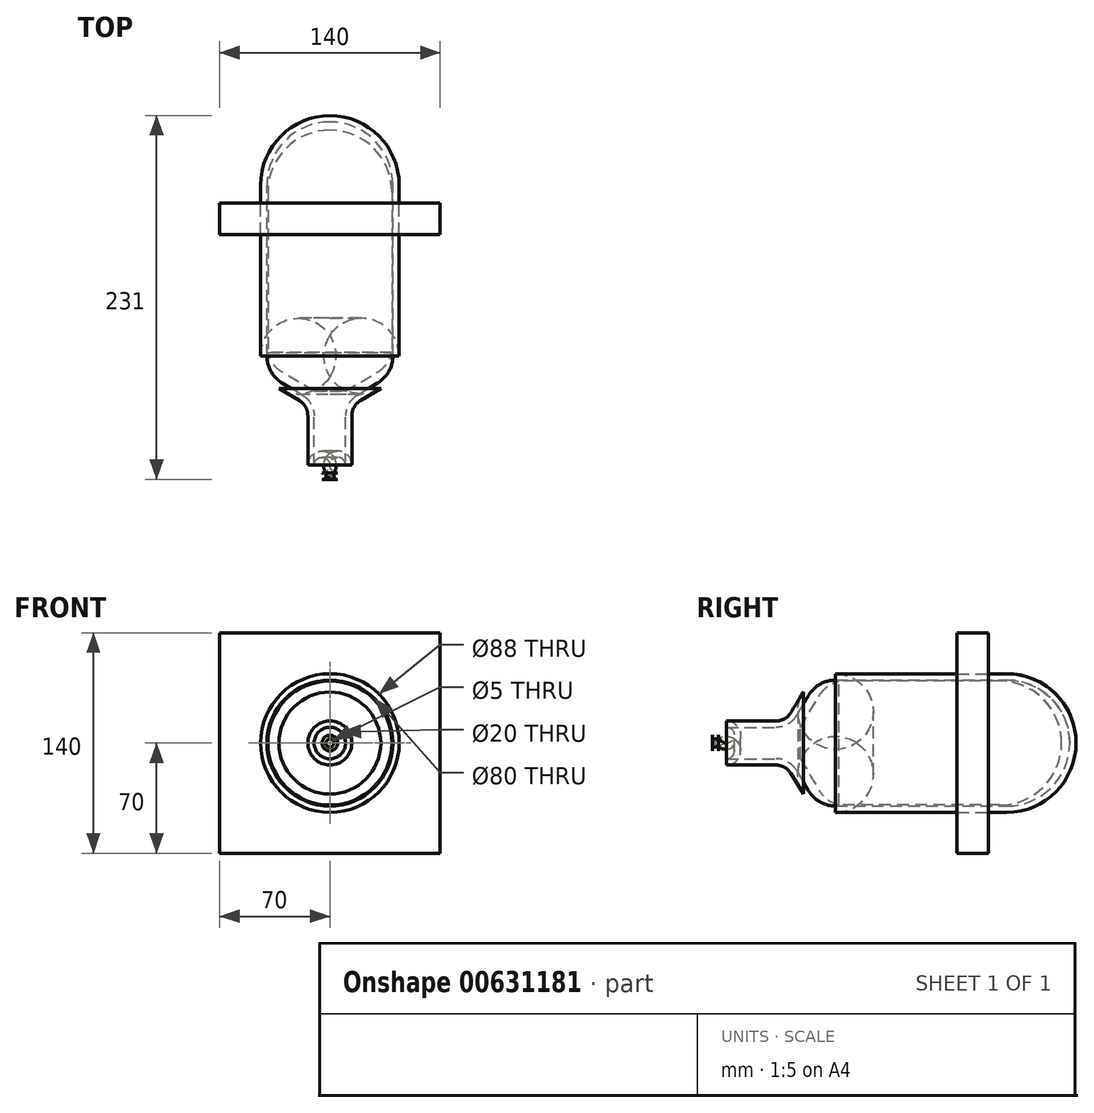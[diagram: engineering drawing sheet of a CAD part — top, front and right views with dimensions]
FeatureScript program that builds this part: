
annotation { "Feature Type Name" : "Feature", "Feature Type Description" : "" }
export const myFeature = defineFeature(function(context is Context, id is Id, definition is map)
    precondition{}
    {
        {
            var Q0;
            Q0=qCreatedBy(makeId("Right.planeOp"),FACE);
            var sketch = newSketch(context, id + "F0", { "sketchPlane" : qUnion([Q0])});
            skLineSegment(sketch, "E0", {"start": v(-160.68, 40) * mm, "end": v(-52, 40) * mm});
            skLineSegment(sketch, "E1", {"start": v(-160.68, -40) * mm, "end": v(-52, -40) * mm});
            skArc(sketch, "E2", {"start": v(-52, -40) * mm, "mid": v(-12, 0) * mm, "end": v(-52, 40) * mm});
            skPoint(sketch, "E3", {"position": v(-12, 0) * mm});
            skLineSegment(sketch, "E4", {"start": v(-177.83, 30.29) * mm, "end": v(-185.63, 17.28) * mm});
            skLineSegment(sketch, "E5", {"start": v(-198.5, 10) * mm, "end": v(-230, 10) * mm});
            skLineSegment(sketch, "E6", {"start": v(-235, 5) * mm, "end": v(-235, 2.5) * mm});
            skLineSegment(sketch, "E7", {"start": v(-230, -10) * mm, "end": v(-198.5, -10) * mm});
            skLineSegment(sketch, "E8", {"start": v(-185.63, -17.28) * mm, "end": v(-177.83, -30.29) * mm});
            skPoint(sketch, "E9.visualSharp", {"position": v(-172, 40) * mm});
            skArc(sketch, "E9.filletArc", {"start": v(-160.68, 40) * mm, "mid": v(-170.53, 37.4) * mm, "end": v(-177.83, 30.29) * mm});
            skPoint(sketch, "E10.visualSharp", {"position": v(-172, -40) * mm});
            skArc(sketch, "E10.filletArc", {"start": v(-177.83, -30.29) * mm, "mid": v(-170.53, -37.4) * mm, "end": v(-160.68, -40) * mm});
            skPoint(sketch, "E11.visualSharp", {"position": v(-190, 10) * mm});
            skArc(sketch, "E11.filletArc", {"start": v(-198.5, 10) * mm, "mid": v(-191.1, 11.95) * mm, "end": v(-185.63, 17.28) * mm});
            skPoint(sketch, "E12.visualSharp", {"position": v(-190, -10) * mm});
            skArc(sketch, "E12.filletArc", {"start": v(-185.63, -17.28) * mm, "mid": v(-191.1, -11.95) * mm, "end": v(-198.5, -10) * mm});
            skPoint(sketch, "E13.visualSharp", {"position": v(-235, 10) * mm});
            skArc(sketch, "E13.filletArc", {"start": v(-230, 10) * mm, "mid": v(-233.54, 8.54) * mm, "end": v(-235, 5) * mm});
            skPoint(sketch, "E14.visualSharp", {"position": v(-235, -10) * mm});
            skArc(sketch, "E14.filletArc", {"start": v(-235, -5) * mm, "mid": v(-233.54, -8.54) * mm, "end": v(-230, -10) * mm});
            skPoint(sketch, "E15", {"position": v(-235, 2.5) * mm});
            skPoint(sketch, "E16", {"position": v(-235, 0) * mm});
            skPoint(sketch, "E17", {"position": v(-235, -2.5) * mm});
            skLineSegment(sketch, "E18.trimOffspring", {"start": v(-235, -2.5) * mm, "end": v(-235, -5) * mm});
            skLineSegment(sketch, "E19.0", {"start": v(-239, 5) * mm, "end": v(-239, 2.5) * mm});
            skArc(sketch, "E19.1", {"start": v(-230, 14) * mm, "mid": v(-236.36, 11.36) * mm, "end": v(-239, 5) * mm});
            skLineSegment(sketch, "E19.2", {"start": v(-198.5, 14) * mm, "end": v(-230, 14) * mm});
            skArc(sketch, "E19.3", {"start": v(-198.5, 14) * mm, "mid": v(-193.07, 15.43) * mm, "end": v(-189.06, 19.34) * mm});
            skLineSegment(sketch, "E19.4", {"start": v(-181.26, 32.35) * mm, "end": v(-189.06, 19.34) * mm});
            skArc(sketch, "E19.5", {"start": v(-189.06, -19.34) * mm, "mid": v(-193.07, -15.43) * mm, "end": v(-198.5, -14) * mm});
            skLineSegment(sketch, "E19.6", {"start": v(-230, -14) * mm, "end": v(-198.5, -14) * mm});
            skArc(sketch, "E19.7", {"start": v(-239, -5) * mm, "mid": v(-236.36, -11.36) * mm, "end": v(-230, -14) * mm});
            skLineSegment(sketch, "E19.8", {"start": v(-239, -2.5) * mm, "end": v(-239, -5) * mm});
            skLineSegment(sketch, "E19.9", {"start": v(-189.06, -19.34) * mm, "end": v(-181.26, -32.35) * mm});
            skArc(sketch, "E19.10", {"start": v(-181.26, -32.35) * mm, "mid": v(-172.5, -40.88) * mm, "end": v(-160.68, -44) * mm});
            skLineSegment(sketch, "E19.11", {"start": v(-160.68, -44) * mm, "end": v(-52, -44) * mm});
            skArc(sketch, "E19.12", {"start": v(-52, -44) * mm, "mid": v(-8, 0) * mm, "end": v(-52, 44) * mm});
            skLineSegment(sketch, "E19.13", {"start": v(-160.68, 44) * mm, "end": v(-52, 44) * mm});
            skArc(sketch, "E19.14", {"start": v(-160.68, 44) * mm, "mid": v(-172.5, 40.88) * mm, "end": v(-181.26, 32.35) * mm});
            skLineSegment(sketch, "E20", {"start": v(-239, 2.5) * mm, "end": v(-235, 2.5) * mm});
            skLineSegment(sketch, "E21", {"start": v(-239, -2.5) * mm, "end": v(-235, -2.5) * mm});
            skLineSegment(sketch, "E22", {"start": v(-52, 0) * mm, "end": v(-72, 0) * mm, "construction": true});
            skLineSegment(sketch, "E23", {"start": v(-12, 0) * mm, "end": v(-8, 0) * mm});
            skPoint(sketch, "E24", {"position": v(0, 0) * mm});
            skSolve(sketch);
        }
        {
            var Q0;
            {var subQ3=sQuery(id+"F0.wireOp",EDGE,"E0");Q0=makeQuery(id+"F0.imprint","IMPRINT",FACE,{"disambiguationData":[TD([[makeQuery(id+"F0.imprint","IMPRINT",EDGE,{"derivedFrom":subQ3}),1.0]])]});}
            var Q1;
            Q1=sQuery(id+"F0.wireOp",EDGE,"E22");
            revolve(context, id + "F1", {"entities" : qUnion([Q0]), "axis" : qUnion([Q1]), "revolveType" : RevolveType.FULL});
        }
        {
            var Q0;
            Q0=qCreatedBy(makeId("Right.planeOp"),FACE);
            var sketch = newSketch(context, id + "F2", { "sketchPlane" : qUnion([Q0])});
            skLineSegment(sketch, "E25", {"start": v(-153.75, 40) * mm, "end": v(-52, 40) * mm, "construction": true});
            skLineSegment(sketch, "E26", {"start": v(-153.75, -40) * mm, "end": v(-52, -40) * mm, "construction": true});
            skArc(sketch, "E27", {"start": v(-52, -40) * mm, "mid": v(-12, 0) * mm, "end": v(-52, 40) * mm, "construction": true});
            skPoint(sketch, "E28", {"position": v(-12, 0) * mm});
            skLineSegment(sketch, "E29", {"start": v(-177.83, 30.29) * mm, "end": v(-185.63, 17.28) * mm, "construction": true});
            skLineSegment(sketch, "E30", {"start": v(-198.5, 10) * mm, "end": v(-230, 10) * mm, "construction": true});
            skLineSegment(sketch, "E31", {"start": v(-235, 5) * mm, "end": v(-235, 2.5) * mm, "construction": true});
            skLineSegment(sketch, "E32", {"start": v(-230, -10) * mm, "end": v(-198.5, -10) * mm, "construction": true});
            skLineSegment(sketch, "E33", {"start": v(-185.63, -17.28) * mm, "end": v(-177.83, -30.29) * mm, "construction": true});
            skPoint(sketch, "E34.visualSharp", {"position": v(-172, 40) * mm});
            skArc(sketch, "E34.filletArc", {"start": v(-160.68, 40) * mm, "mid": v(-170.53, 37.4) * mm, "end": v(-177.83, 30.29) * mm, "construction": true});
            skPoint(sketch, "E35.visualSharp", {"position": v(-172, -40) * mm});
            skArc(sketch, "E35.filletArc", {"start": v(-177.83, -30.29) * mm, "mid": v(-170.53, -37.4) * mm, "end": v(-160.68, -40) * mm, "construction": true});
            skPoint(sketch, "E36.visualSharp", {"position": v(-190, 10) * mm});
            skArc(sketch, "E36.filletArc", {"start": v(-198.5, 10) * mm, "mid": v(-191.1, 11.95) * mm, "end": v(-185.63, 17.28) * mm, "construction": true});
            skPoint(sketch, "E37.visualSharp", {"position": v(-190, -10) * mm});
            skArc(sketch, "E37.filletArc", {"start": v(-185.63, -17.28) * mm, "mid": v(-191.1, -11.95) * mm, "end": v(-198.5, -10) * mm, "construction": true});
            skPoint(sketch, "E38.visualSharp", {"position": v(-235, 10) * mm});
            skArc(sketch, "E38.filletArc", {"start": v(-230, 10) * mm, "mid": v(-233.54, 8.54) * mm, "end": v(-235, 5) * mm, "construction": true});
            skPoint(sketch, "E39.visualSharp", {"position": v(-235, -10) * mm});
            skArc(sketch, "E39.filletArc", {"start": v(-235, -5) * mm, "mid": v(-233.54, -8.54) * mm, "end": v(-230, -10) * mm, "construction": true});
            skPoint(sketch, "E40", {"position": v(-235, 2.5) * mm});
            skPoint(sketch, "E41", {"position": v(-235, 0) * mm});
            skPoint(sketch, "E42", {"position": v(-235, -2.5) * mm});
            skLineSegment(sketch, "E43.trimOffspring", {"start": v(-235, -2.5) * mm, "end": v(-235, -5) * mm, "construction": true});
            skLineSegment(sketch, "E44.0", {"start": v(-239, 5) * mm, "end": v(-239, 2.5) * mm, "construction": true});
            skArc(sketch, "E44.1", {"start": v(-230, 14) * mm, "mid": v(-236.36, 11.36) * mm, "end": v(-239, 5) * mm, "construction": true});
            skLineSegment(sketch, "E44.2", {"start": v(-198.5, 14) * mm, "end": v(-230, 14) * mm, "construction": true});
            skArc(sketch, "E44.3", {"start": v(-198.5, 14) * mm, "mid": v(-193.07, 15.43) * mm, "end": v(-189.06, 19.34) * mm, "construction": true});
            skLineSegment(sketch, "E44.4", {"start": v(-181.26, 32.35) * mm, "end": v(-189.06, 19.34) * mm, "construction": true});
            skArc(sketch, "E44.5", {"start": v(-189.06, -19.34) * mm, "mid": v(-193.07, -15.43) * mm, "end": v(-198.5, -14) * mm, "construction": true});
            skLineSegment(sketch, "E44.6", {"start": v(-230, -14) * mm, "end": v(-198.5, -14) * mm, "construction": true});
            skArc(sketch, "E44.7", {"start": v(-239, -5) * mm, "mid": v(-236.36, -11.36) * mm, "end": v(-230, -14) * mm, "construction": true});
            skLineSegment(sketch, "E44.8", {"start": v(-239, -2.5) * mm, "end": v(-239, -5) * mm, "construction": true});
            skLineSegment(sketch, "E44.9", {"start": v(-189.06, -19.34) * mm, "end": v(-181.26, -32.35) * mm, "construction": true});
            skArc(sketch, "E44.10", {"start": v(-181.26, -32.35) * mm, "mid": v(-172.5, -40.88) * mm, "end": v(-160.68, -44) * mm, "construction": true});
            skLineSegment(sketch, "E44.11", {"start": v(-160.68, -44) * mm, "end": v(-52, -44) * mm, "construction": true});
            skArc(sketch, "E44.12", {"start": v(-52, -44) * mm, "mid": v(-8, 0) * mm, "end": v(-52, 44) * mm, "construction": true});
            skLineSegment(sketch, "E44.13", {"start": v(-160.68, 44) * mm, "end": v(-52, 44) * mm, "construction": true});
            skArc(sketch, "E44.14", {"start": v(-160.68, 44) * mm, "mid": v(-172.5, 40.88) * mm, "end": v(-181.26, 32.35) * mm, "construction": true});
            skLineSegment(sketch, "E45", {"start": v(-239, 2.5) * mm, "end": v(-235, 2.5) * mm, "construction": true});
            skLineSegment(sketch, "E46", {"start": v(-239, -2.5) * mm, "end": v(-235, -2.5) * mm, "construction": true});
            skLineSegment(sketch, "E47", {"start": v(-12, 0) * mm, "end": v(-8, 0) * mm, "construction": true});
            skPoint(sketch, "E48", {"position": v(0, 0) * mm});
            skLineSegment(sketch, "E49", {"start": v(-8, 0) * mm, "end": v(0, 0) * mm, "construction": true});
            skLineSegment(sketch, "E50", {"start": v(-158.6, 39.4) * mm, "end": v(-56.6, 39.4) * mm});
            skLineSegment(sketch, "E51", {"start": v(-56.6, -39.4) * mm, "end": v(-158.6, -39.4) * mm});
            skArc(sketch, "E52", {"start": v(-56.6, -39.4) * mm, "mid": v(-17.2, 0) * mm, "end": v(-56.6, 39.4) * mm});
            skLineSegment(sketch, "E53", {"start": v(-170.9, 30.27) * mm, "end": v(-183.04, 10) * mm});
            skLineSegment(sketch, "E54", {"start": v(-183.04, 10) * mm, "end": v(-183.04, -10) * mm});
            skLineSegment(sketch, "E55", {"start": v(-183.04, -10) * mm, "end": v(-170.9, -30.27) * mm});
            skLineSegment(sketch, "E56", {"start": v(-183.04, -10) * mm, "end": v(-170.9, -30.27) * mm, "construction": true});
            skArc(sketch, "E57.filletArc", {"start": v(-170.9, -30.27) * mm, "mid": v(-165.67, -36.06) * mm, "end": v(-158.6, -39.4) * mm, "construction": true});
            skPoint(sketch, "E58", {"position": v(-158.6, -39.4) * mm});
            skArc(sketch, "E59", {"start": v(-158.6, -39.4) * mm, "mid": v(-165.67, -36.06) * mm, "end": v(-170.9, -30.27) * mm});
            skPoint(sketch, "E60.orphan", {"position": v(-165.44, -39.4) * mm});
            skLineSegment(sketch, "E61", {"start": v(-183.04, 10) * mm, "end": v(-170.9, 30.27) * mm, "construction": true});
            skArc(sketch, "E62.filletArc", {"start": v(-158.6, 39.4) * mm, "mid": v(-165.67, 36.06) * mm, "end": v(-170.9, 30.27) * mm, "construction": true});
            skPoint(sketch, "E63", {"position": v(-158.6, 39.4) * mm});
            skArc(sketch, "E64", {"start": v(-170.9, 30.27) * mm, "mid": v(-165.67, 36.06) * mm, "end": v(-158.6, 39.4) * mm});
            skPoint(sketch, "E65.orphan", {"position": v(-165.44, 39.4) * mm});
            skPoint(sketch, "E66", {"position": v(-17.2, 0) * mm});
            skLineSegment(sketch, "E67", {"start": v(-153.75, 40) * mm, "end": v(-160.68, 40) * mm, "construction": true});
            skLineSegment(sketch, "E68", {"start": v(-160.68, -40) * mm, "end": v(-153.75, -40) * mm, "construction": true});
            skLineSegment(sketch, "E69", {"start": v(-17.2, 0) * mm, "end": v(-183.04, 0) * mm});
            skSolve(sketch);
        }
        {
            var Q0;
            Q0=qCreatedBy(makeId("Front.planeOp"),FACE);
            cPlane(context, id + "F3", {"entities" : qUnion([Q0]), "cplaneType" : CPlaneType.OFFSET, "offset" : 63.54 * mm, "width" : 150 * mm, "height" : 150 * mm});
        }
        {
            var Q0;
            Q0=qCreatedBy(id+"F3.planeOp",FACE);
            var sketch = newSketch(context, id + "F4", { "sketchPlane" : qUnion([Q0])});
            skCircle(sketch, "E70", {"center": v(0, 0) * mm, "radius": 44 * mm});
            skLineSegment(sketch, "E71", {"start": v(-70, 70) * mm, "end": v(70, 70) * mm});
            skLineSegment(sketch, "E72", {"start": v(70, 70) * mm, "end": v(70, -70) * mm});
            skLineSegment(sketch, "E73", {"start": v(70, -70) * mm, "end": v(-70, -70) * mm});
            skLineSegment(sketch, "E74", {"start": v(-70, -70) * mm, "end": v(-70, 70) * mm});
            skSolve(sketch);
        }
        {
            var Q0;
            Q0=makeQuery(id+"F4.imprint","IMPRINT",FACE,{"disambiguationData":[TD([[makeQuery(id+"F4.imprint","IMPRINT",EDGE,{"derivedFrom":sQuery(id+"F4.wireOp",EDGE,"E70")}),-1.0]])]});
            extrude(context, id + "F5", {"entities" : qUnion([Q0]), "depth" : 20 * mm, "offsetDistance" : 25 * mm});
        }
        {
            var Q0;
            {var subQ2=sQuery(id+"F2.wireOp",EDGE,"E50");Q0=makeQuery(id+"F2.imprint","IMPRINT",FACE,{"disambiguationData":[TD([[makeQuery(id+"F2.imprint","IMPRINT",EDGE,{"derivedFrom":subQ2}),-1.0]])]});}
            var Q1;
            Q1=sQuery(id+"F2.wireOp",EDGE,"E49");
            revolve(context, id + "F6", {"entities" : qUnion([Q0]), "axis" : qUnion([Q1]), "revolveType" : RevolveType.FULL});
        }
    });
